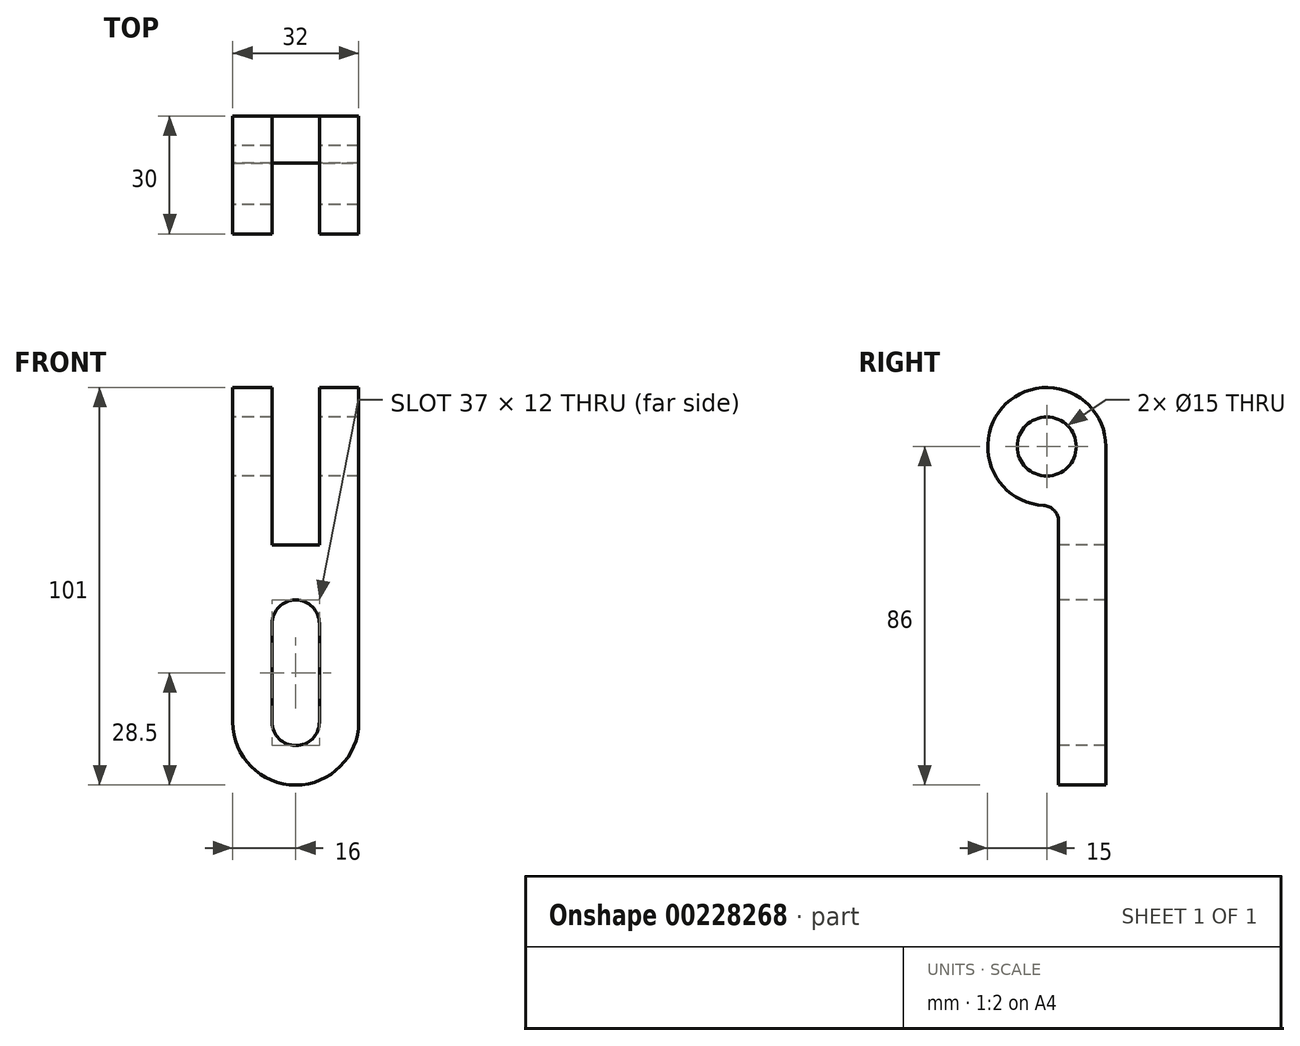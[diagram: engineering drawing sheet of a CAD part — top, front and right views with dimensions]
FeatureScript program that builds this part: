
annotation { "Feature Type Name" : "Feature", "Feature Type Description" : "" }
export const myFeature = defineFeature(function(context is Context, id is Id, definition is map)
    precondition{}
    {
        {
            var Q0;
            Q0=qCreatedBy(makeId("Right.planeOp"),FACE);
            var sketch = newSketch(context, id + "F0", { "sketchPlane" : qUnion([Q0])});
            skCircle(sketch, "E0", {"center": v(0, 0) * mm, "radius": 7.5 * mm});
            skArc(sketch, "E1", {"start": v(15, 0) * mm, "mid": v(-10.32, 10.88) * mm, "end": v(-0.79, -14.98) * mm});
            skLineSegment(sketch, "E2", {"start": v(15, 0) * mm, "end": v(15, -86) * mm});
            skLineSegment(sketch, "E3", {"start": v(15, -86) * mm, "end": v(3, -86) * mm});
            skLineSegment(sketch, "E4", {"start": v(3, -86) * mm, "end": v(3, -18.97) * mm});
            skPoint(sketch, "E5.visualSharp", {"position": v(3, -14.7) * mm});
            skArc(sketch, "E5.filletArc", {"start": v(3, -18.97) * mm, "mid": v(1.9, -16.22) * mm, "end": v(-0.79, -14.98) * mm});
            skSolve(sketch);
        }
        {
            var Q0;
            Q0 = qSketchRegion(id + "F0", true);
            extrude(context, id + "F1", {"entities" : qUnion([Q0]), "depth" : 32 * mm});
        }
        {
            var Q0;
            Q0=qCreatedBy(makeId("Front.planeOp"),FACE);
            var sketch = newSketch(context, id + "F2", { "sketchPlane" : qUnion([Q0])});
            skLineSegment(sketch, "E6", {"start": v(0, 15) * mm, "end": v(32, 15) * mm, "construction": true});
            skLineSegment(sketch, "E7.0", {"start": v(32, 15) * mm, "end": v(32, -14.98) * mm, "construction": true});
            skLineSegment(sketch, "E8.0", {"start": v(0, 15) * mm, "end": v(0, -14.98) * mm, "construction": true});
            skPoint(sketch, "E9.0", {"position": v(0, -16.22) * mm});
            skPoint(sketch, "E10.0", {"position": v(32, -16.22) * mm});
            skLineSegment(sketch, "E11.0", {"start": v(32, -86) * mm, "end": v(32, -18.97) * mm, "construction": true});
            skLineSegment(sketch, "E12.0", {"start": v(0, -86) * mm, "end": v(0, -18.97) * mm, "construction": true});
            skPoint(sketch, "E13.0", {"position": v(16, -86) * mm});
            skLineSegment(sketch, "E14.0", {"start": v(32, -86) * mm, "end": v(0, -86) * mm, "construction": true});
            skLineSegment(sketch, "E15", {"start": v(10, 15) * mm, "end": v(10, -25) * mm});
            skLineSegment(sketch, "E16", {"start": v(10, -25) * mm, "end": v(22, -25) * mm});
            skLineSegment(sketch, "E17", {"start": v(22, -25) * mm, "end": v(22, 15) * mm});
            skLineSegment(sketch, "E18", {"start": v(22, 15) * mm, "end": v(10, 15) * mm});
            skSolve(sketch);
        }
        {
            var Q0;
            Q0 = qSketchRegion(id + "F2", true);
            extrude(context, id + "F3", {"entities" : qUnion([Q0]), "operationType" : NewBodyOperationType.REMOVE, "endBound" : BoundingType.SYMMETRIC, "oppositeDirection" : true, "depth" : 47.1 * mm});
        }
        {
            var Q0;
            Q0=qCreatedBy(makeId("Front.planeOp"),FACE);
            var sketch = newSketch(context, id + "F4", { "sketchPlane" : qUnion([Q0])});
            skLineSegment(sketch, "E19.0.0", {"start": v(22, -25) * mm, "end": v(22, 0) * mm, "construction": true});
            skLineSegment(sketch, "E19.0.1", {"start": v(22, 0) * mm, "end": v(32, 0) * mm, "construction": true});
            skLineSegment(sketch, "E19.0.2", {"start": v(32, 0) * mm, "end": v(32, -59.73) * mm, "construction": true});
            skLineSegment(sketch, "E19.0.3", {"start": v(32, -86) * mm, "end": v(0, -86) * mm, "construction": true});
            skLineSegment(sketch, "E19.0.5", {"start": v(0, 0) * mm, "end": v(10, 0) * mm, "construction": true});
            skLineSegment(sketch, "E19.0.6", {"start": v(10, 0) * mm, "end": v(10, -25) * mm, "construction": true});
            skLineSegment(sketch, "E19.0.7", {"start": v(10, -25) * mm, "end": v(22, -25) * mm, "construction": true});
            skLineSegment(sketch, "E20", {"start": v(22, 15) * mm, "end": v(32, 15) * mm, "construction": true});
            skLineSegment(sketch, "E21", {"start": v(0, 15) * mm, "end": v(10, 15) * mm, "construction": true});
            skArc(sketch, "E22", {"start": v(0, -70) * mm, "mid": v(16, -86) * mm, "end": v(32, -70) * mm});
            skPoint(sketch, "E22.centerSnap0", {"position": v(16, -25) * mm});
            skLineSegment(sketch, "E23", {"start": v(32, -70) * mm, "end": v(32, -86) * mm});
            skLineSegment(sketch, "E24", {"start": v(0, -86) * mm, "end": v(0, -70) * mm});
            skLineSegment(sketch, "E25.trimOffspring", {"start": v(0, -55.89) * mm, "end": v(0, 0) * mm, "construction": true});
            skLineSegment(sketch, "E26", {"start": v(32, -86) * mm, "end": v(0, -86) * mm});
            skArc(sketch, "E27", {"start": v(22, -45) * mm, "mid": v(16, -39) * mm, "end": v(10, -45) * mm});
            skArc(sketch, "E28", {"start": v(10, -70) * mm, "mid": v(16, -76) * mm, "end": v(22, -70) * mm});
            skLineSegment(sketch, "E29", {"start": v(22, -45) * mm, "end": v(22, -70) * mm});
            skLineSegment(sketch, "E30", {"start": v(10, -45) * mm, "end": v(10, -70) * mm});
            skSolve(sketch);
        }
        {
            var Q0;
            {var subQ0=sQuery(id+"F4.wireOp",EDGE,"E24");Q0=makeQuery(id+"F4.imprint","IMPRINT",FACE,{"disambiguationData":[TD([[makeQuery(id+"F4.imprint","IMPRINT",EDGE,{"derivedFrom":subQ0}),-1.0]])]});}
            var Q1;
            Q1=makeQuery(id+"F4.imprint","IMPRINT",FACE,{"disambiguationData":[TD([[makeQuery(id+"F4.imprint","IMPRINT",EDGE,{"derivedFrom":sQuery(id+"F4.wireOp",EDGE,"E27")}),1.0]])]});
            var Q2;
            Q2=makeQuery(id+"F1.opExtrude","SWEPT_FACE",FACE,{"disambiguationData":[OSD([sQuery(id+"F0.wireOp",EDGE,"E2")])]});
            var Q3;
            {var subQ0=sQuery(id+"F4.wireOp",EDGE,"E23");Q3=makeQuery(id+"F4.imprint","IMPRINT",FACE,{"disambiguationData":[TD([[makeQuery(id+"F4.imprint","IMPRINT",EDGE,{"derivedFrom":subQ0}),-1.0]])]});}
            extrude(context, id + "F5", {"entities" : qUnion([Q0, Q1, Q2, Q3]), "operationType" : NewBodyOperationType.REMOVE, "endBound" : BoundingType.THROUGH_ALL, "oppositeDirection" : true, "depth" : 25 * mm});
        }
    });
